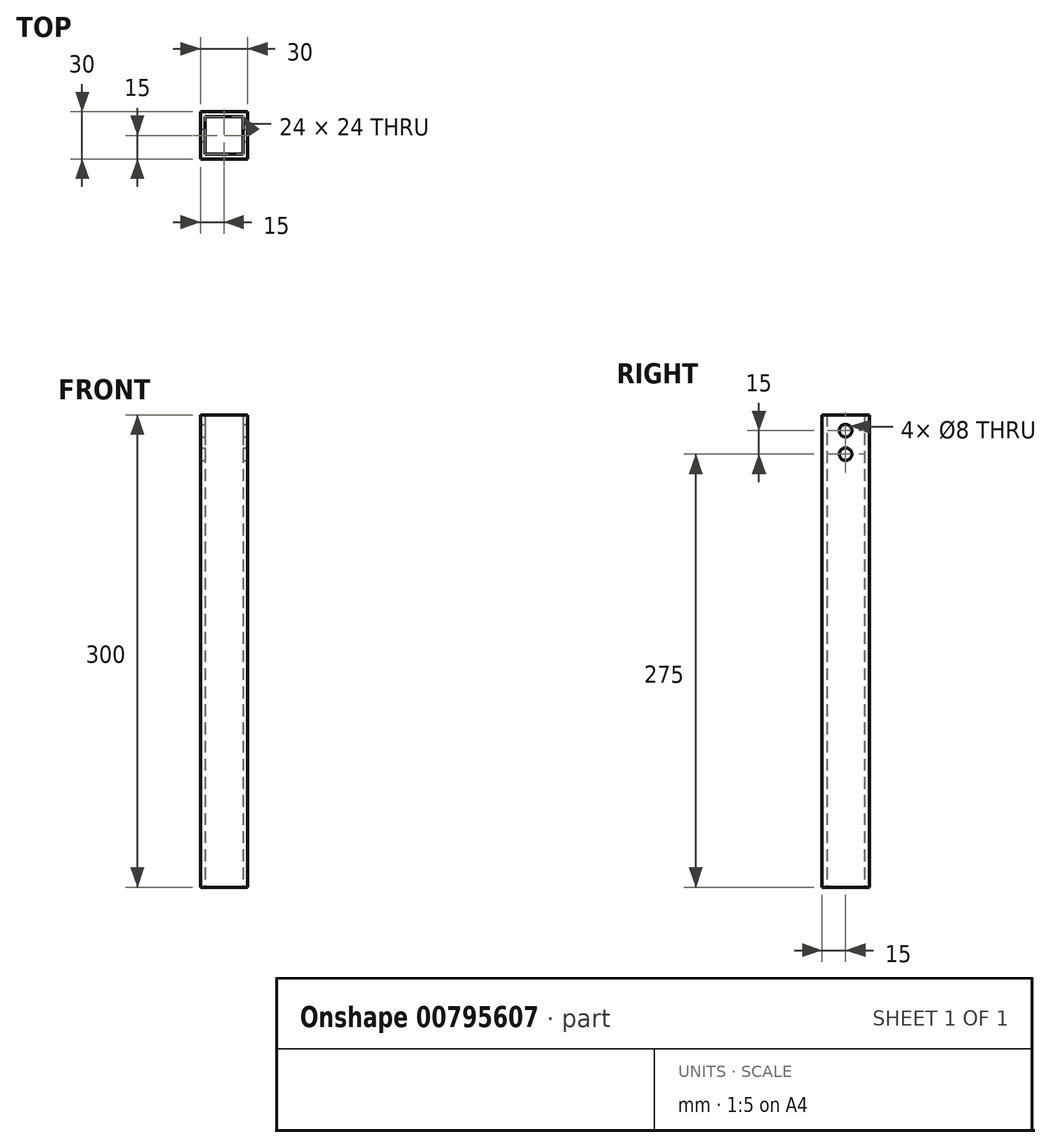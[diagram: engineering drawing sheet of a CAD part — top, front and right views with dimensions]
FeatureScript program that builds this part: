
annotation { "Feature Type Name" : "Feature", "Feature Type Description" : "" }
export const myFeature = defineFeature(function(context is Context, id is Id, definition is map)
    precondition{}
    {
        {
            var Q0;
            Q0=qCreatedBy(makeId("Top.planeOp"),FACE);
            var sketch = newSketch(context, id + "F0", { "sketchPlane" : qUnion([Q0])});
            skLineSegment(sketch, "E0.bottom", {"start": v(15, -15) * mm, "end": v(-15, -15) * mm});
            skLineSegment(sketch, "E0.top", {"start": v(15, 15) * mm, "end": v(-15, 15) * mm});
            skLineSegment(sketch, "E0.left", {"start": v(15, -15) * mm, "end": v(15, 15) * mm});
            skLineSegment(sketch, "E0.right", {"start": v(-15, -15) * mm, "end": v(-15, 15) * mm});
            skPoint(sketch, "E0.middle", {"position": v(0, 0) * mm});
            skLineSegment(sketch, "E1.bottom", {"start": v(12, -12) * mm, "end": v(-12, -12) * mm});
            skLineSegment(sketch, "E1.top", {"start": v(12, 12) * mm, "end": v(-12, 12) * mm});
            skLineSegment(sketch, "E1.left", {"start": v(12, -12) * mm, "end": v(12, 12) * mm});
            skLineSegment(sketch, "E1.right", {"start": v(-12, -12) * mm, "end": v(-12, 12) * mm});
            skSolve(sketch);
        }
        {
            var Q0;
            Q0=makeQuery(id+"F0.imprint","IMPRINT",FACE,{"disambiguationData":[TD([[makeQuery(id+"F0.imprint","IMPRINT",EDGE,{"derivedFrom":sQuery(id+"F0.wireOp",EDGE,"E0.bottom")}),-1.0]])]});
            extrude(context, id + "F1", {"entities" : qUnion([Q0]), "endBound" : BoundingType.SYMMETRIC, "depth" : 300 * mm, "offsetDistance" : 25 * mm});
        }
        {
            var Q0;
            Q0=makeQuery(id+"F1.opExtrude","SWEPT_FACE",FACE,{"disambiguationData":[OSD([sQuery(id+"F0.wireOp",EDGE,"E0.left")])]});
            var sketch = newSketch(context, id + "F2", { "sketchPlane" : qUnion([Q0])});
            skCircle(sketch, "E2", {"center": v(0, 140) * mm, "radius": 4 * mm});
            skCircle(sketch, "E3", {"center": v(0, 125) * mm, "radius": 4 * mm});
            skLineSegment(sketch, "E4", {"start": v(-15, 109) * mm, "end": v(15, 109) * mm, "construction": true});
            skSolve(sketch);
        }
        {
            var Q0;
            Q0=sQuery(id+"F2.wireOp",VERTEX,"E2.center");
            var Q1;
            Q1=sQuery(id+"F2.wireOp",VERTEX,"E3.center");
            var Q2;
            Q2=makeQuery(id+"F1.opExtrude","SWEPT_BODY",BODY,{"disambiguationData":[OSD([sQuery(id+"F0.wireOp",EDGE,"E0.bottom"),sQuery(id+"F0.wireOp",EDGE,"E0.top"),sQuery(id+"F0.wireOp",EDGE,"E0.left"),sQuery(id+"F0.wireOp",EDGE,"E0.right"),sQuery(id+"F0.wireOp",EDGE,"E1.bottom"),sQuery(id+"F0.wireOp",EDGE,"E1.top"),sQuery(id+"F0.wireOp",EDGE,"E1.left"),sQuery(id+"F0.wireOp",EDGE,"E1.right")])]});
            hole(context, id + "F3", {"style" : HoleStyle.SIMPLE, "endStyle" : HoleEndStyle.THROUGH, "standardTappedOrClearance" : lookupTablePath({ "standard" : "ISO", "size" : "8", "type" : "Drilled" }), "standardBlindInLast" : lookupTablePath({ "standard" : "ISO", "size" : "8", "type" : "Drilled" }), "holeDiameter" : 8 * mm, "majorDiameter" : 5 * mm, "isTappedThrough" : true, "tappedDepth" : 12.7 * mm, "tapClearance" : 3, "locations" : qUnion([Q0, Q1]), "scope" : qUnion([Q2])});
        }
    });
